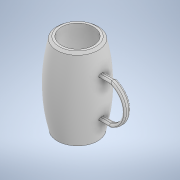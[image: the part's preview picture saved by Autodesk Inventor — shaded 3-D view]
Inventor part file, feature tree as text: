
AUTODESK INVENTOR PART (.ipt)
format: ipt  version: 2020 (Build 240168000, 168)  size: 225,792 bytes
history: native  units: mm
features: sketch x2, revolve x1, shell x1, extrude x1, fillet x1, chamfer x1
ambient origin geometry x8: Origin, YZ Plane, XZ Plane, XY Plane, X Axis, Y Axis, Z Axis, Center Point
bodies: Solid1 (feature_tree)
feature tree (7):
  revolve  "Revolution1"  [1 undecoded]
  shell  "Shell1"  Thickness=25.0mm
  extrude  "Extrusion1"  TaperAngle=90.0deg  [1 undecoded]
  fillet  "Fillet1"  Radius=4.0mm
  chamfer  "Chamfer1"  Distance=30.0mm
  sketch  "Sketch2"  dims[d4=34.0mm d6=45.0mm d7=25.0mm]
  sketch  "Sketch4"  dims[d8=80.0mm d9=90.0deg d10=4.0mm d11=30.0mm d12=40.0mm d13=3.0mm d14=6.0mm d15=0.0mm d16=2.0mm d17=2.0mm d18=2.0mm d19=45.0deg]
note: 2 required parameter values undecoded (feature->parameter linkage not recoverable at this tier; creation-order binding heuristic only, values carry confidence <= 0.55)